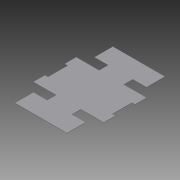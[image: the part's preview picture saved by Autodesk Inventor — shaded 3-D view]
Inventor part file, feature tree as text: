
AUTODESK INVENTOR PART (.ipt)
format: ipt  version: 2015 SP1 (Build 190203100, 203)  size: 144,384 bytes
history: native  units: in
note: dims shown in document units (in); Inventor stores cm internally (conversion verified against a paired STEP export)
features: extrude x2, sketch x2, projected_geometry x1
ambient origin geometry x8: Origin, YZ Plane, XZ Plane, XY Plane, X Axis, Y Axis, Z Axis, Center Point
bodies: Solid1 (feature_tree)
feature tree (5):
  extrude  "Extrusion1"  Depth=32.0in
  extrude  "Extrusion2"  Depth=6.5in
  sketch  "Sketch1"  dims[d0=23.0in d1=32.0in]
  sketch  "Sketch2"  dims[d2=0.125in d3=0.0in d4=6.5in d5=6.5in d6=1.0in d7=1.0in d8=12.75in d9=12.75in d10=3.0in d11=9.0in d12=3.0in d13=9.0in d14=3.0in d15=9.0in d16=3.0in d17=9.0in d18=4.5in d19=3.0in d20=4.5in d21=3.0in d22=4.5in d23=3.0in d24=4.5in d25=3.0in d26=0.125in d27=0.0in]
  projected_geometry  "Projected Loop1"
